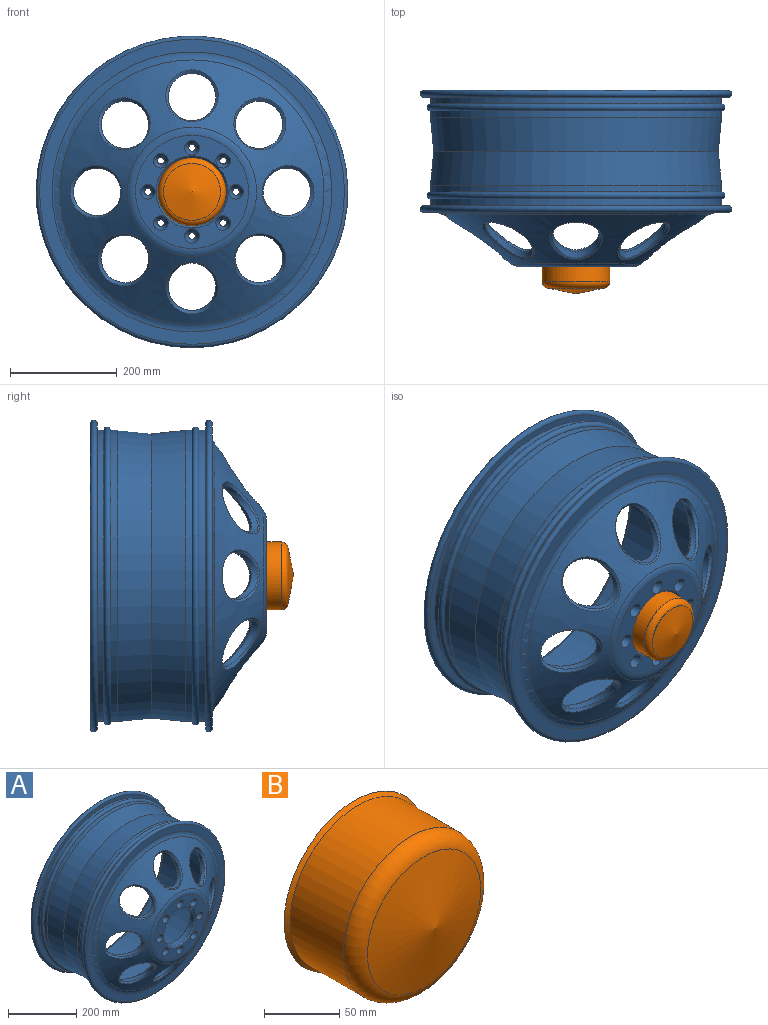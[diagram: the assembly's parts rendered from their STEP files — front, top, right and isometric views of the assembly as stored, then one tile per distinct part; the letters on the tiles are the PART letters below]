
ASSEMBLY  parts=2 mates=1
PART A: 67 faces, bbox 632.3x330.2x632.3 mm
  f0: cylinder r=273.05mm len=546.1mm, axis (0,1,0), area 21788.4mm2, adj f30,f32
  f1: cylinder r=273.05mm len=546.1mm, axis (0,-1,0), area 21788.4mm2, adj f27,f33
  f2: cylinder r=6.35mm len=12.7mm, axis (0,1,0), area 506.7mm2, adj f12,f64
  f3: cylinder r=6.35mm len=12.7mm, axis (0,1,0), area 506.7mm2, adj f12,f63
  f4: cylinder r=6.35mm len=12.7mm, axis (0,1,0), area 506.7mm2, adj f12,f62
  f5: cylinder r=6.35mm len=12.7mm, axis (0,1,0), area 506.7mm2, adj f12,f61
  f6: cylinder r=6.35mm len=12.7mm, axis (0,1,0), area 506.7mm2, adj f12,f60
  f7: cylinder r=6.35mm len=12.7mm, axis (0,1,0), area 506.7mm2, adj f12,f59
  f8: cylinder r=6.35mm len=12.7mm, axis (0,1,0), area 506.7mm2, adj f12,f66
  f9: cylinder r=6.35mm len=12.7mm, axis (0,1,0), area 506.7mm2, adj f12,f65
  f10: cylinder r=63.5mm len=127mm, axis (0,1,0), area 6890.5mm2, adj f49,f50
  f11: plane 212.08x212.08mm, normal (0,-1,0), area 16279.4mm2, adj f39,f49,f59,f60,f61,f62,f63,f64
  f12: plane 220.13x220.13mm, normal (0,1,0), area 22704.6mm2, adj f2,f3,f4,f5,f6,f7,f8,f9
  f13: cylinder r=44.45mm len=88.9mm, axis (0,1,0), area 3669.9mm2, adj f45,f53
  f14: cylinder r=44.45mm len=88.9mm, axis (0,1,0), area 3864.8mm2, adj f46,f54
  f15: cylinder r=44.45mm len=88.9mm, axis (0,1,0), area 3873.5mm2, adj f41,f55
  f16: cylinder r=44.45mm len=88.9mm, axis (0,1,0), area 4049.8mm2, adj f43,f56
  f17: cylinder r=44.45mm len=88.9mm, axis (0,1,0), area 3802.2mm2, adj f42,f57
  f18: cylinder r=44.45mm len=88.9mm, axis (0,1,0), area 3956mm2, adj f44,f58
  f19: cylinder r=44.45mm len=88.9mm, axis (0,1,0), area 4088.2mm2, adj f48,f51
  f20: cylinder r=44.45mm len=88.9mm, axis (0,1,0), area 3803mm2, adj f47,f52
  f21: cone r=114.3mm half-angle=54deg, axis (0,1,0), area 106873.1mm2, adj f38,f39,f51,f52,f53,f54,f55,f56
  f22: cone r=254mm half-angle=53.1deg, axis (0,1,0), area 98853.4mm2, adj f37,f40,f41,f42,f43,f44,f45,f46
  f23: cylinder r=254mm len=508mm, axis (0,1,0), area 293890.3mm2, adj f36,f40
  f24: plane 571.5x571.5mm, normal (0,-1,0), area 40441.5mm2, adj f35,f38
  f25: plane 571.5x571.5mm, normal (0,1,0), area 43576.8mm2, adj f34,f36
  f26: plane 571.5x571.5mm, normal (0,1,0), area 22295.1mm2, adj f29,f35
  f27: plane 571.5x571.5mm, normal (0,-1,0), area 22295.1mm2, adj f1,f34
  f28: cylinder r=273.05mm len=546.1mm, axis (0,-1,0), area 21788.4mm2, adj f31,f33
  f29: cylinder r=273.05mm len=546.1mm, axis (0,1,0), area 21788.4mm2, adj f26,f32
  f30: cone r=273.05mm half-angle=5.7deg, axis (0,-1,0), area 108212.4mm2, adj f0,f31
  f31: cone r=266.7mm half-angle=5.7deg, axis (0,1,0), area 108212.4mm2, adj f28,f30
  f32: torus R=273.05mm, axis (0,-1,0), area 34731.9mm2, adj f0,f29
  f33: torus R=273.05mm, axis (0,-1,0), area 34731.9mm2, adj f1,f28
  f34: torus R=285.75mm, axis (0,-1,0), area 36323.7mm2, adj f25,f27
  f35: torus R=285.75mm, axis (0,-1,0), area 36323.7mm2, adj f24,f26
  f36: torus R=260.35mm, axis (0,-1,0), area 16063.3mm2, adj f23,f25
  f37: torus R=110.07mm, axis (0,-1,0), area 12114.4mm2, adj f12,f22
  f38: torus R=262.26mm, axis (0,-1,0), area 25542.8mm2, adj f21,f24
  f39: torus R=106.04mm, axis (0,-1,0), area 11416.6mm2, adj f11,f21
  f40: torus R=228.6mm, axis (0,-1,0), area 37073.4mm2, adj f22,f23
  f41: bspline ~96.92x95.62mm, area 1785mm2, adj f15,f22
  f42: bspline ~97.05x95.84mm, area 1785.4mm2, adj f17,f22
  f43: bspline ~96.3x96.27mm, area 1785mm2, adj f16,f22
  f44: bspline ~96.31x96.28mm, area 1785.1mm2, adj f18,f22
  f45: bspline ~97.03x95.9mm, area 1785mm2, adj f13,f22
  f46: bspline ~96.23x96.22mm, area 1785.1mm2, adj f14,f22
  f47: bspline ~96.45x96.45mm, area 1785mm2, adj f20,f22
  f48: bspline ~97.14x95.88mm, area 1785mm2, adj f19,f22
  f49: cone r=63.5mm half-angle=45deg, axis (0,-1,0), area 2367mm2, adj f10,f11
  f50: cone r=67.56mm half-angle=45deg, axis (0,1,0), area 2367mm2, adj f10,f12
  f51: bspline ~98.42x97.06mm, area 1937.8mm2, adj f19,f21
  f52: bspline ~97.87x97.83mm, area 1938.2mm2, adj f20,f21
  f53: bspline ~98.29x96.91mm, area 1937.7mm2, adj f13,f21
  f54: bspline ~97.92x97.86mm, area 1937.6mm2, adj f14,f21
  f55: bspline ~98.35x97.11mm, area 1938.1mm2, adj f15,f21
  f56: bspline ~97.7x97.68mm, area 1937.1mm2, adj f16,f21
  f57: bspline ~98.38x97.04mm, area 1938.3mm2, adj f17,f21
  f58: bspline ~97.7x97.69mm, area 1937.7mm2, adj f18,f21
  f59: cone r=6.35mm half-angle=30deg, axis (0,-1,0), area 922.9mm2, adj f7,f11
  f60: cone r=6.35mm half-angle=30deg, axis (0,-1,0), area 922.9mm2, adj f6,f11
  f61: cone r=6.35mm half-angle=30deg, axis (0,-1,0), area 922.9mm2, adj f5,f11
  f62: cone r=6.35mm half-angle=30deg, axis (0,-1,0), area 922.9mm2, adj f4,f11
  f63: cone r=6.35mm half-angle=30deg, axis (0,-1,0), area 922.9mm2, adj f3,f11
  f64: cone r=6.35mm half-angle=30deg, axis (0,-1,0), area 922.9mm2, adj f2,f11
  f65: cone r=6.35mm half-angle=30deg, axis (0,-1,0), area 922.9mm2, adj f9,f11
  f66: cone r=6.35mm half-angle=30deg, axis (0,-1,0), area 922.9mm2, adj f8,f11
PART B: 8 faces, bbox 137.5x76.2x137.5 mm
  f0: plane 132.49x132.49mm, normal (0,1,0), area 1792.9mm2, adj f1,f7
  f1: cylinder r=61.79mm len=123.57mm, axis (0,1,0), area 20609.5mm2, adj f0,f3
  f2: cone r=63.16mm half-angle=78.7deg, axis (0,1,0), area 8984mm2, adj f3
  f3: torus R=50.8mm, axis (0,-1,0), area 5559.3mm2, adj f1,f2
  f4: cone r=63.5mm half-angle=78.7deg, axis (0,1,0), area 9098.5mm2, adj f5
  f5: torus R=50.8mm, axis (0,-1,0), area 6561mm2, adj f4,f6
  f6: cylinder r=63.5mm len=127mm, axis (0,1,0), area 20086.9mm2, adj f5,f7
  f7: cone r=62.33mm half-angle=45deg, axis (0,1,0), area 1581.3mm2, adj f0,f6
PLACE A at identity
PLACE B t=(0,-101.6,0)mm
MATE fastened B.f1 <-> A.f10  axis (0,1,0) through (0,-101.6,0)mm
